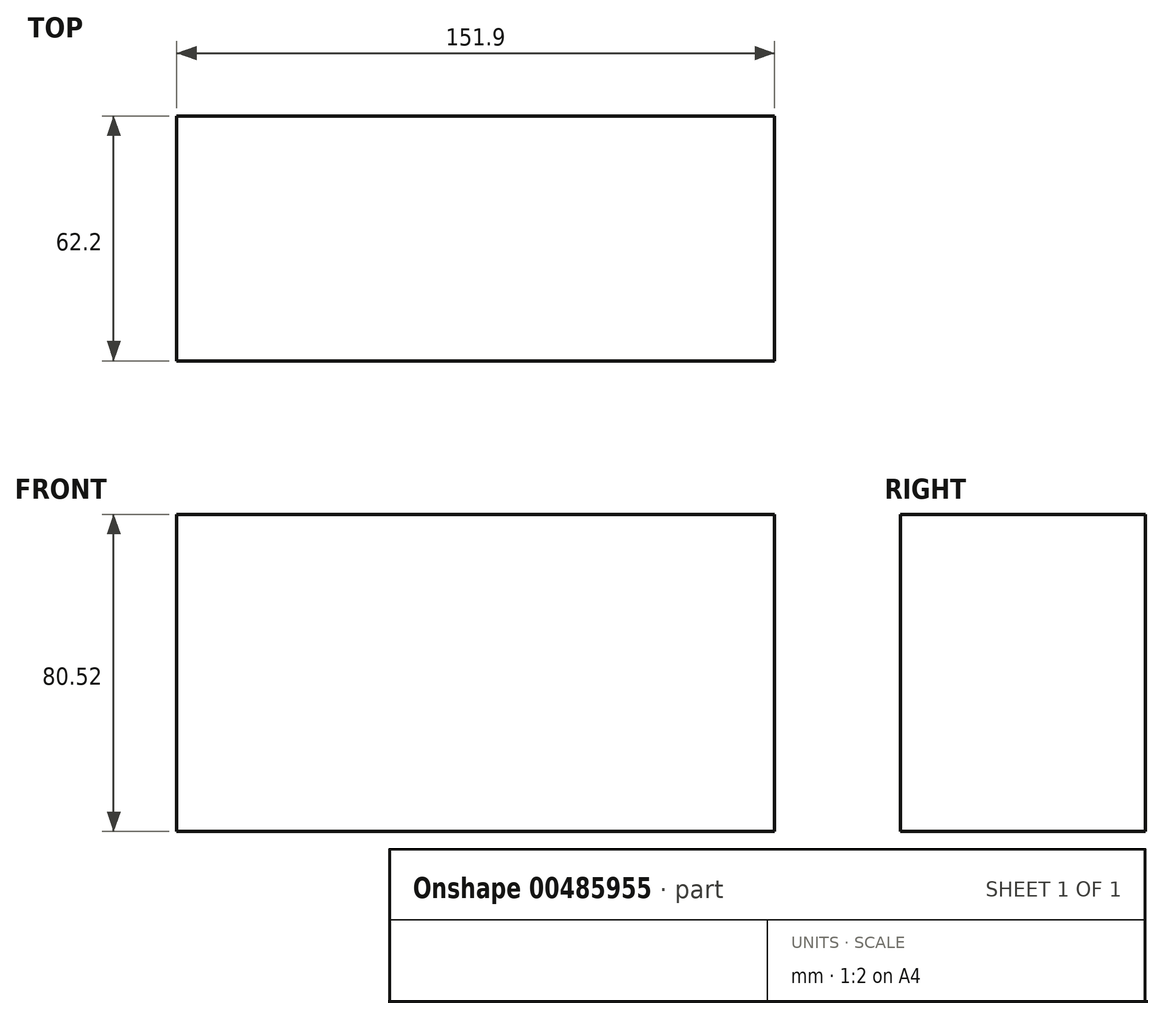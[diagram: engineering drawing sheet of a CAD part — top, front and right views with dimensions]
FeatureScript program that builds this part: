
annotation { "Feature Type Name" : "Feature", "Feature Type Description" : "" }
export const myFeature = defineFeature(function(context is Context, id is Id, definition is map)
    precondition{}
    {
        {
            var Q0;
            Q0=qCreatedBy(makeId("Top.planeOp"),FACE);
            var sketch = newSketch(context, id + "F0", { "sketchPlane" : qUnion([Q0])});
            skLineSegment(sketch, "E0.bottom", {"start": v(-89.48, 26.34) * mm, "end": v(62.42, 26.34) * mm});
            skLineSegment(sketch, "E0.top", {"start": v(-89.48, -35.86) * mm, "end": v(62.42, -35.86) * mm});
            skLineSegment(sketch, "E0.left", {"start": v(-89.48, 26.34) * mm, "end": v(-89.48, -35.86) * mm});
            skLineSegment(sketch, "E0.right", {"start": v(62.42, 26.34) * mm, "end": v(62.42, -35.86) * mm});
            skSolve(sketch);
        }
        {
            var Q0;
            Q0=makeQuery(id+"F0.imprint","IMPRINT",FACE,{"disambiguationData":[TD([[makeQuery(id+"F0.imprint","IMPRINT",EDGE,{"derivedFrom":sQuery(id+"F0.wireOp",EDGE,"E0.bottom")}),-1.0]])]});
            extrude(context, id + "F1", {"entities" : qUnion([Q0]), "depth" : 80.52 * mm});
        }
    });
